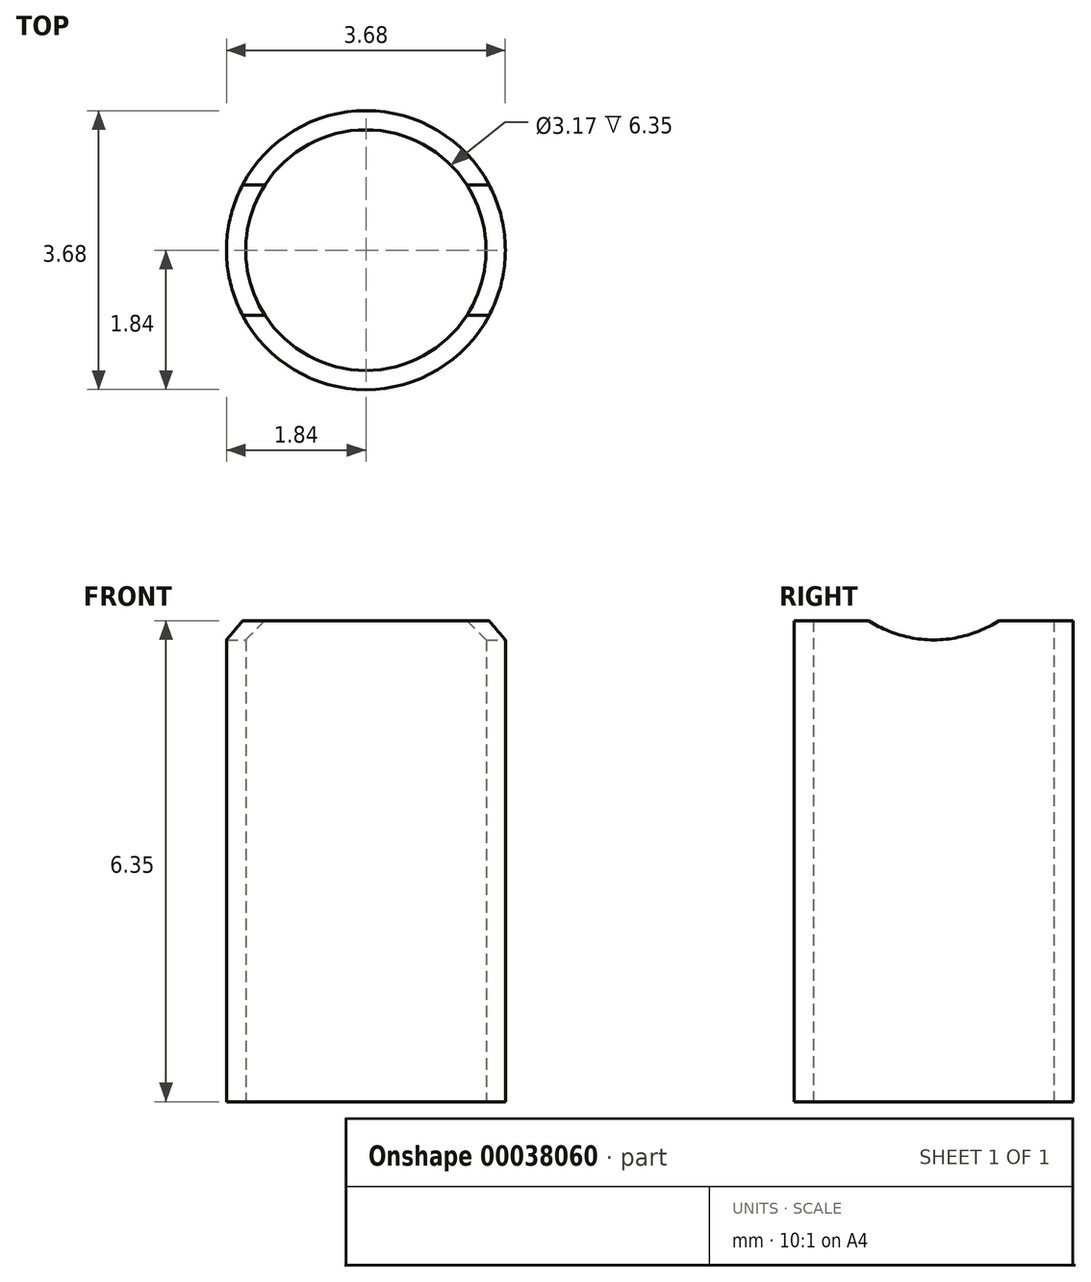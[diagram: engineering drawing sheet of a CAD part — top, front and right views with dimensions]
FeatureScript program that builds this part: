
annotation { "Feature Type Name" : "Feature", "Feature Type Description" : "" }
export const myFeature = defineFeature(function(context is Context, id is Id, definition is map)
    precondition{}
    {
        {
            var Q0;
            Q0=qCreatedBy(makeId("Top.planeOp"),FACE);
            var sketch = newSketch(context, id + "F0", { "sketchPlane" : qUnion([Q0])});
            skLineSegment(sketch, "E0.rect.bottom", {"start": v(1.84, -1.84) * mm, "end": v(-1.84, -1.84) * mm});
            skLineSegment(sketch, "E0.rect.top", {"start": v(1.84, 1.84) * mm, "end": v(-1.84, 1.84) * mm});
            skLineSegment(sketch, "E0.rect.left", {"start": v(1.84, -1.84) * mm, "end": v(1.84, 1.84) * mm});
            skLineSegment(sketch, "E0.rect.right", {"start": v(-1.84, -1.84) * mm, "end": v(-1.84, 1.84) * mm});
            skPoint(sketch, "E0.rect.middle", {"position": v(0, 0) * mm});
            skCircle(sketch, "E1", {"center": v(0, 0) * mm, "radius": 1.59 * mm});
            skSolve(sketch);
        }
        {
            var Q0;
            Q0=qSketchRegion(id+"F0",true);
            extrude(context, id + "F1", {"entities" : qUnion([Q0]), "depth" : 6.35 * mm});
        }
        {
            var Q0;
            Q0=makeQuery(id+"F1.opExtrude","SWEPT_FACE",FACE,{"disambiguationData":[OSD([sQuery(id+"F0.wireOp",EDGE,"E0.rect.left")])]});
            var sketch = newSketch(context, id + "F2", { "sketchPlane" : qUnion([Q0])});
            skArc(sketch, "E2", {"start": v(-0.86, 6.35) * mm, "mid": v(0, 6.1) * mm, "end": v(0.86, 6.35) * mm});
            skLineSegment(sketch, "E3", {"start": v(0, 6.35) * mm, "end": v(0, 7.68) * mm, "construction": true});
            skPoint(sketch, "E3.endSnap0", {"position": v(0, 6.35) * mm});
            skLineSegment(sketch, "E4", {"start": v(0, 6.35) * mm, "end": v(0, 6.1) * mm, "construction": true});
            skLineSegment(sketch, "E5", {"start": v(-0.86, 6.35) * mm, "end": v(0.86, 6.35) * mm});
            skSolve(sketch);
        }
        {
            var Q0;
            Q0=qSketchRegion(id+"F2",true);
            var Q1;
            Q1=makeQuery(id+"F1.opExtrude","SWEPT_FACE",FACE,{"disambiguationData":[OSD([sQuery(id+"F0.wireOp",EDGE,"E0.rect.right")])]});
            extrude(context, id + "F3", {"entities" : qUnion([Q0]), "operationType" : NewBodyOperationType.REMOVE, "endBound" : BoundingType.UP_TO_SURFACE, "oppositeDirection" : true, "endBoundEntityFace" : qUnion([Q1]), "depth" : 25.4 * mm});
        }
        {
            var Q0;
            Q0=makeQuery(id+"F1.opExtrude","SWEPT_EDGE",EDGE,{"disambiguationData":[OSD([sQuery(id+"F0.wireOp",EDGE,"E0.rect.bottom"),sQuery(id+"F0.wireOp",EDGE,"E0.rect.right")])]});
            var Q1;
            Q1=makeQuery(id+"F1.opExtrude","SWEPT_EDGE",EDGE,{"disambiguationData":[OSD([sQuery(id+"F0.wireOp",EDGE,"E0.rect.bottom"),sQuery(id+"F0.wireOp",EDGE,"E0.rect.left")])]});
            var Q2;
            Q2=makeQuery(id+"F1.opExtrude","SWEPT_EDGE",EDGE,{"disambiguationData":[OSD([sQuery(id+"F0.wireOp",EDGE,"E0.rect.top"),sQuery(id+"F0.wireOp",EDGE,"E0.rect.right")])]});
            var Q3;
            Q3=makeQuery(id+"F1.opExtrude","SWEPT_EDGE",EDGE,{"disambiguationData":[OSD([sQuery(id+"F0.wireOp",EDGE,"E0.rect.top"),sQuery(id+"F0.wireOp",EDGE,"E0.rect.left")])]});
            fillet(context, id + "F4", {"entities" : qUnion([Q0, Q1, Q2, Q3]), "radius" : 1.84 * mm, "tangentPropagation" : true, "allowEdgeOverflow" : false});
        }
    });
